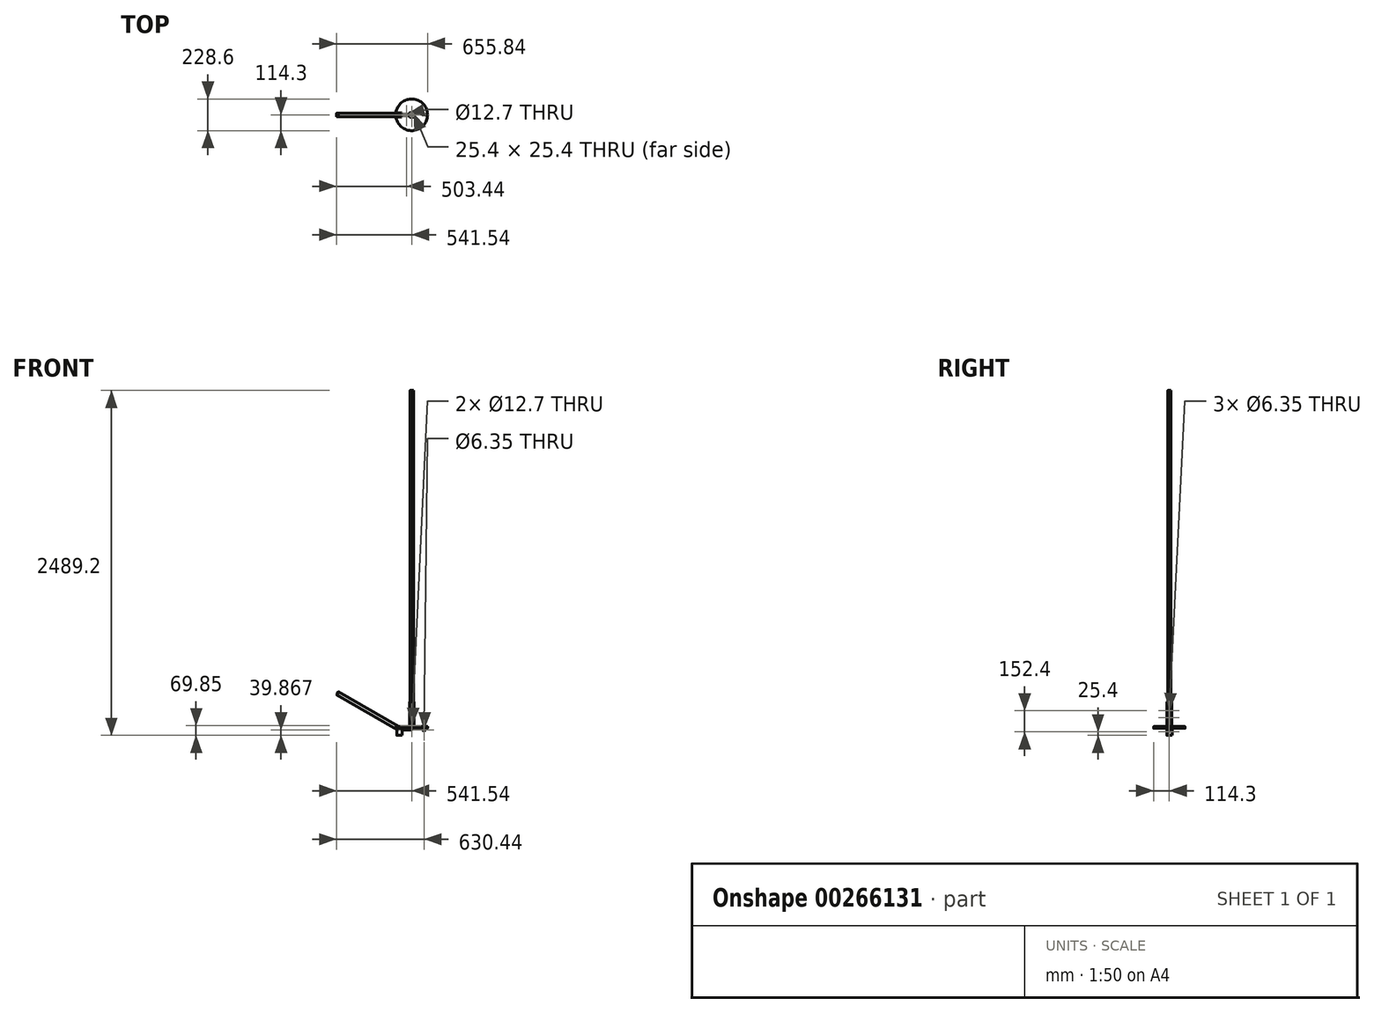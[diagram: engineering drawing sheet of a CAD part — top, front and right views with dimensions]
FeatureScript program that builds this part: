
annotation { "Feature Type Name" : "Feature", "Feature Type Description" : "" }
export const myFeature = defineFeature(function(context is Context, id is Id, definition is map)
    precondition{}
    {
        {
            var Q0;
            Q0=qCreatedBy(makeId("Right.planeOp"),FACE);
            var sketch = newSketch(context, id + "F16", { "sketchPlane" : qUnion([Q0])});
            skLineSegment(sketch, "E0", {"start": v(12.7, 9.53) * mm, "end": v(12.7, -9.53) * mm});
            skLineSegment(sketch, "E1", {"start": v(9.53, -12.7) * mm, "end": v(-9.53, -12.7) * mm});
            skLineSegment(sketch, "E2", {"start": v(-12.7, -9.53) * mm, "end": v(-12.7, 9.53) * mm});
            skLineSegment(sketch, "E3", {"start": v(-9.52, 12.7) * mm, "end": v(9.52, 12.7) * mm});
            skPoint(sketch, "E4.visualSharp", {"position": v(-12.7, 12.7) * mm});
            skArc(sketch, "E4.filletArc", {"start": v(-9.52, 12.7) * mm, "mid": v(-11.77, 11.77) * mm, "end": v(-12.7, 9.53) * mm});
            skPoint(sketch, "E5.visualSharp", {"position": v(12.7, 12.7) * mm});
            skArc(sketch, "E5.filletArc", {"start": v(12.7, 9.53) * mm, "mid": v(11.77, 11.77) * mm, "end": v(9.52, 12.7) * mm});
            skPoint(sketch, "E6.visualSharp", {"position": v(12.7, -12.7) * mm});
            skArc(sketch, "E6.filletArc", {"start": v(9.53, -12.7) * mm, "mid": v(11.77, -11.77) * mm, "end": v(12.7, -9.53) * mm});
            skPoint(sketch, "E7.visualSharp", {"position": v(-12.7, -12.7) * mm});
            skArc(sketch, "E7.filletArc", {"start": v(-12.7, -9.53) * mm, "mid": v(-11.77, -11.77) * mm, "end": v(-9.53, -12.7) * mm});
            skLineSegment(sketch, "E8.0", {"start": v(-9.52, 9.53) * mm, "end": v(9.52, 9.53) * mm});
            skLineSegment(sketch, "E9.0", {"start": v(9.53, 9.53) * mm, "end": v(9.53, -9.53) * mm});
            skLineSegment(sketch, "E10.0", {"start": v(-9.53, -9.53) * mm, "end": v(-9.53, 9.53) * mm});
            skLineSegment(sketch, "E11.0", {"start": v(9.52, -9.53) * mm, "end": v(-9.53, -9.53) * mm});
            skSolve(sketch);
        }
        {
            var Q0;
            Q0=qCreatedBy(makeId("Front.planeOp"),FACE);
            var sketch = newSketch(context, id + "F0", { "sketchPlane" : qUnion([Q0])});
            skLineSegment(sketch, "E12", {"start": v(0, 0) * mm, "end": v(0, -12.7) * mm, "construction": true});
            skLineSegment(sketch, "E13", {"start": v(0, -12.7) * mm, "end": v(-94.8, -12.7) * mm});
            skLineSegment(sketch, "E14", {"start": v(-107.5, -9.3) * mm, "end": v(-541.54, 241.3) * mm});
            skPoint(sketch, "E15.visualSharp", {"position": v(-101.6, -12.7) * mm});
            skArc(sketch, "E15.filletArc", {"start": v(-107.5, -9.3) * mm, "mid": v(-101.37, -11.83) * mm, "end": v(-94.8, -12.7) * mm});
            skSolve(sketch);
        }
        {
            var Q0;
            Q0=makeQuery(id+"F16.imprint","IMPRINT",FACE,{"disambiguationData":[TD([[makeQuery(id+"F16.imprint","IMPRINT",EDGE,{"derivedFrom":sQuery(id+"F16.wireOp",EDGE,"E0")}),-1.0]])]});
            var Q1;
            Q1=sQuery(id+"F0.wireOp",EDGE,"E13");
            var Q2;
            Q2=sQuery(id+"F0.wireOp",EDGE,"E15.filletArc");
            var Q3;
            Q3=sQuery(id+"F0.wireOp",EDGE,"E14");
            sweep(context, id + "F1", {"profiles" : qUnion([Q0]), "path" : qUnion([Q1, Q2, Q3])});
        }
        {
            var Q0;
            Q0=makeQuery(id+"F1.opSweep","SWEPT_FACE",FACE,{"disambiguationData":[OSD([sQuery(id+"F16.wireOp",EDGE,"E2"),sQuery(id+"F0.wireOp",EDGE,"E14")])]});
            var sketch = newSketch(context, id + "F17", { "sketchPlane" : qUnion([Q0])});
            skCircle(sketch, "E16", {"center": v(-518.7, 242.77) * mm, "radius": 4.13 * mm});
            skCircle(sketch, "E17", {"center": v(-463.7, 211.02) * mm, "radius": 4.13 * mm});
            skLineSegment(sketch, "E18", {"start": v(-539.95, 244.05) * mm, "end": v(-530.43, 260.55) * mm, "construction": true});
            skSolve(sketch);
        }
        {
            var Q0;
            Q0=makeQuery(id+"F17.imprint","IMPRINT",FACE,{"disambiguationData":[TD([[makeQuery(id+"F17.imprint","IMPRINT",EDGE,{"derivedFrom":sQuery(id+"F17.wireOp",EDGE,"E16")}),1.0]])]});
            var Q1;
            Q1=makeQuery(id+"F17.imprint","IMPRINT",FACE,{"disambiguationData":[TD([[makeQuery(id+"F17.imprint","IMPRINT",EDGE,{"derivedFrom":sQuery(id+"F17.wireOp",EDGE,"E17")}),1.0]])]});
            extrude(context, id + "F2", {"entities" : qUnion([Q0, Q1]), "operationType" : NewBodyOperationType.REMOVE, "oppositeDirection" : true, "depth" : 25.4 * mm});
        }
        {
            var Q0;
            Q0=makeQuery(id+"F1.opSweep","SWEPT_FACE",FACE,{"disambiguationData":[OSD([sQuery(id+"F16.wireOp",EDGE,"E3"),sQuery(id+"F0.wireOp",EDGE,"E13")])]});
            var sketch = newSketch(context, id + "F3", { "sketchPlane" : qUnion([Q0])});
            skCircle(sketch, "E19", {"center": v(-38.1, 0) * mm, "radius": 6.35 * mm});
            skSolve(sketch);
        }
        {
            var Q0;
            Q0=makeQuery(id+"F3.imprint","IMPRINT",FACE,{"disambiguationData":[TD([[makeQuery(id+"F3.imprint","IMPRINT",EDGE,{"derivedFrom":sQuery(id+"F3.wireOp",EDGE,"E19")}),1.0]])]});
            extrude(context, id + "F18", {"entities" : qUnion([Q0]), "operationType" : NewBodyOperationType.REMOVE, "oppositeDirection" : true, "depth" : 25.4 * mm});
        }
        {
            var Q0;
            Q0=qCreatedBy(makeId("Top.planeOp"),FACE);
            var sketch = newSketch(context, id + "F4", { "sketchPlane" : qUnion([Q0])});
            skLineSegment(sketch, "E20", {"start": v(12.7, 15.88) * mm, "end": v(-12.7, 15.88) * mm});
            skLineSegment(sketch, "E21", {"start": v(-15.87, 12.7) * mm, "end": v(-15.87, -12.7) * mm});
            skLineSegment(sketch, "E22", {"start": v(-12.7, -15.88) * mm, "end": v(12.7, -15.87) * mm});
            skLineSegment(sketch, "E23", {"start": v(15.88, -12.7) * mm, "end": v(15.88, 12.7) * mm});
            skPoint(sketch, "E24.visualSharp", {"position": v(-15.87, 15.88) * mm});
            skArc(sketch, "E24.filletArc", {"start": v(-12.7, 15.87) * mm, "mid": v(-14.95, 14.95) * mm, "end": v(-15.87, 12.7) * mm});
            skPoint(sketch, "E25.visualSharp", {"position": v(15.88, 15.88) * mm});
            skArc(sketch, "E25.filletArc", {"start": v(15.88, 12.7) * mm, "mid": v(14.95, 14.95) * mm, "end": v(12.7, 15.88) * mm});
            skPoint(sketch, "E26.visualSharp", {"position": v(15.88, -15.87) * mm});
            skArc(sketch, "E26.filletArc", {"start": v(12.7, -15.87) * mm, "mid": v(14.95, -14.95) * mm, "end": v(15.88, -12.7) * mm});
            skPoint(sketch, "E27.visualSharp", {"position": v(-15.87, -15.87) * mm});
            skArc(sketch, "E27.filletArc", {"start": v(-15.87, -12.7) * mm, "mid": v(-14.95, -14.95) * mm, "end": v(-12.7, -15.88) * mm});
            skLineSegment(sketch, "E28.0", {"start": v(12.7, 12.7) * mm, "end": v(-12.7, 12.7) * mm});
            skLineSegment(sketch, "E29.0", {"start": v(12.7, -12.7) * mm, "end": v(12.7, 12.7) * mm});
            skLineSegment(sketch, "E30.0", {"start": v(-12.7, -12.7) * mm, "end": v(12.7, -12.7) * mm});
            skLineSegment(sketch, "E31.0", {"start": v(-12.7, 12.7) * mm, "end": v(-12.7, -12.7) * mm});
            skSolve(sketch);
        }
        {
            var Q0;
            Q0=makeQuery(id+"F4.imprint","IMPRINT",FACE,{"disambiguationData":[TD([[makeQuery(id+"F4.imprint","IMPRINT",EDGE,{"derivedFrom":sQuery(id+"F4.wireOp",EDGE,"E20")}),1.0]])]});
            extrude(context, id + "F5", {"entities" : qUnion([Q0]), "depth" : 190.5 * mm});
        }
        {
            var Q0;
            Q0=makeQuery(id+"F5.opExtrude","SWEPT_FACE",FACE,{"disambiguationData":[OSD([sQuery(id+"F4.wireOp",EDGE,"E22")])]});
            var sketch = newSketch(context, id + "F6", { "sketchPlane" : qUnion([Q0])});
            skCircle(sketch, "E32", {"center": v(0, 19.05) * mm, "radius": 6.35 * mm});
            skSolve(sketch);
        }
        {
            var Q0;
            Q0=makeQuery(id+"F6.imprint","IMPRINT",FACE,{"disambiguationData":[TD([[makeQuery(id+"F6.imprint","IMPRINT",EDGE,{"derivedFrom":sQuery(id+"F6.wireOp",EDGE,"E32")}),1.0]])]});
            extrude(context, id + "F19", {"entities" : qUnion([Q0]), "operationType" : NewBodyOperationType.REMOVE, "oppositeDirection" : true, "depth" : 31.75 * mm});
        }
        {
            var Q0;
            Q0=makeQuery(id+"F5.opExtrude","SWEPT_FACE",FACE,{"disambiguationData":[OSD([sQuery(id+"F4.wireOp",EDGE,"E21")])]});
            var sketch = newSketch(context, id + "F7", { "sketchPlane" : qUnion([Q0])});
            skCircle(sketch, "E33", {"center": v(0, 127) * mm, "radius": 3.18 * mm});
            skCircle(sketch, "E34", {"center": v(0, 76.2) * mm, "radius": 3.18 * mm});
            skSolve(sketch);
        }
        {
            var Q0;
            Q0=makeQuery(id+"F7.imprint","IMPRINT",FACE,{"disambiguationData":[TD([[makeQuery(id+"F7.imprint","IMPRINT",EDGE,{"derivedFrom":sQuery(id+"F7.wireOp",EDGE,"E33")}),1.0]])]});
            var Q1;
            Q1=makeQuery(id+"F7.imprint","IMPRINT",FACE,{"disambiguationData":[TD([[makeQuery(id+"F7.imprint","IMPRINT",EDGE,{"derivedFrom":sQuery(id+"F7.wireOp",EDGE,"E34")}),1.0]])]});
            extrude(context, id + "F8", {"entities" : qUnion([Q0, Q1]), "operationType" : NewBodyOperationType.REMOVE, "oppositeDirection" : true, "depth" : 3.17 * mm});
        }
        {
            var Q0;
            Q0=qCreatedBy(makeId("Top.planeOp"),FACE);
            var sketch = newSketch(context, id + "F9", { "sketchPlane" : qUnion([Q0])});
            skCircle(sketch, "E35", {"center": v(0, 0) * mm, "radius": 114.3 * mm});
            skLineSegment(sketch, "E36", {"start": v(-101.6, 12.7) * mm, "end": v(-76.2, 12.7) * mm});
            skLineSegment(sketch, "E37", {"start": v(-76.2, 12.7) * mm, "end": v(-76.2, -12.7) * mm});
            skLineSegment(sketch, "E38", {"start": v(-76.2, -12.7) * mm, "end": v(-101.6, -12.7) * mm});
            skLineSegment(sketch, "E39", {"start": v(-101.6, -12.7) * mm, "end": v(-101.6, 12.7) * mm});
            skLineSegment(sketch, "E40", {"start": v(-104.78, 15.88) * mm, "end": v(-73.03, 15.88) * mm, "construction": true});
            skLineSegment(sketch, "E41", {"start": v(-73.03, 15.88) * mm, "end": v(-73.03, -15.87) * mm, "construction": true});
            skLineSegment(sketch, "E42", {"start": v(-73.03, -15.87) * mm, "end": v(-104.78, -15.88) * mm, "construction": true});
            skLineSegment(sketch, "E43", {"start": v(-104.78, -15.88) * mm, "end": v(-104.78, 15.88) * mm, "construction": true});
            skSolve(sketch);
        }
        {
            var Q0;
            Q0=makeQuery(id+"F9.imprint","IMPRINT",FACE,{"disambiguationData":[TD([[makeQuery(id+"F9.imprint","IMPRINT",EDGE,{"derivedFrom":sQuery(id+"F9.wireOp",EDGE,"E35")}),1.0]])]});
            extrude(context, id + "F10", {"entities" : qUnion([Q0]), "depth" : 12.7 * mm});
        }
        {
            var Q0;
            Q0=makeQuery(id+"F10.opExtrude","CAP_FACE",FACE,{"disambiguationData":[OSD([sQuery(id+"F9.wireOp",EDGE,"E35"),sQuery(id+"F9.wireOp",EDGE,"E36"),sQuery(id+"F9.wireOp",EDGE,"E37"),sQuery(id+"F9.wireOp",EDGE,"E38"),sQuery(id+"F9.wireOp",EDGE,"E39")])],"isStart":true});
            var sketch = newSketch(context, id + "F20", { "sketchPlane" : qUnion([Q0])});
            skLineSegment(sketch, "E44", {"start": v(-104.78, 15.88) * mm, "end": v(-73.03, 15.88) * mm});
            skLineSegment(sketch, "E45", {"start": v(-73.03, 15.88) * mm, "end": v(-73.03, -15.87) * mm});
            skLineSegment(sketch, "E46", {"start": v(-73.03, -15.88) * mm, "end": v(-104.78, -15.88) * mm});
            skLineSegment(sketch, "E47", {"start": v(-104.78, -15.88) * mm, "end": v(-104.78, 15.88) * mm});
            skLineSegment(sketch, "E48", {"start": v(-69.85, -19.05) * mm, "end": v(-107.95, -19.05) * mm});
            skLineSegment(sketch, "E49", {"start": v(-107.95, -19.05) * mm, "end": v(-107.95, 19.05) * mm});
            skLineSegment(sketch, "E50", {"start": v(-107.95, 19.05) * mm, "end": v(-69.85, 19.05) * mm});
            skLineSegment(sketch, "E51", {"start": v(-69.85, 19.05) * mm, "end": v(-69.85, -19.05) * mm});
            skSolve(sketch);
        }
        {
            var Q0;
            Q0=makeQuery(id+"F20.imprint","IMPRINT",FACE,{"disambiguationData":[TD([[makeQuery(id+"F20.imprint","IMPRINT",EDGE,{"derivedFrom":sQuery(id+"F20.wireOp",EDGE,"E44")}),1.0]])]});
            extrude(context, id + "F11", {"entities" : qUnion([Q0]), "operationType" : NewBodyOperationType.ADD, "depth" : 50.8 * mm});
        }
        {
            var Q0;
            Q0=makeQuery(id+"F11.opExtrude","SWEPT_FACE",FACE,{"disambiguationData":[OSD([sQuery(id+"F20.wireOp",EDGE,"E49")])]});
            var sketch = newSketch(context, id + "F12", { "sketchPlane" : qUnion([Q0])});
            skCircle(sketch, "E52", {"center": v(0, -25.4) * mm, "radius": 3.18 * mm});
            skSolve(sketch);
        }
        {
            var Q0;
            Q0=makeQuery(id+"F12.imprint","IMPRINT",FACE,{"disambiguationData":[TD([[makeQuery(id+"F12.imprint","IMPRINT",EDGE,{"derivedFrom":sQuery(id+"F12.wireOp",EDGE,"E52")}),1.0]])]});
            extrude(context, id + "F21", {"entities" : qUnion([Q0]), "operationType" : NewBodyOperationType.REMOVE, "oppositeDirection" : true, "depth" : 3.17 * mm});
        }
        {
            var Q0;
            Q0=makeQuery(id+"F11.opExtrude","SWEPT_EDGE",EDGE,{"disambiguationData":[OSD([sQuery(id+"F20.wireOp",EDGE,"E48"),sQuery(id+"F20.wireOp",EDGE,"E49")])]});
            var Q1;
            Q1=makeQuery(id+"F11.opExtrude","SWEPT_EDGE",EDGE,{"disambiguationData":[OSD([sQuery(id+"F20.wireOp",EDGE,"E49"),sQuery(id+"F20.wireOp",EDGE,"E50")])]});
            var Q2;
            Q2=makeQuery(id+"F11.opExtrude","SWEPT_EDGE",EDGE,{"disambiguationData":[OSD([sQuery(id+"F20.wireOp",EDGE,"E48"),sQuery(id+"F20.wireOp",EDGE,"E51")])]});
            var Q3;
            Q3=makeQuery(id+"F11.opExtrude","SWEPT_EDGE",EDGE,{"disambiguationData":[OSD([sQuery(id+"F20.wireOp",EDGE,"E50"),sQuery(id+"F20.wireOp",EDGE,"E51")])]});
            var Q4;
            Q4=makeQuery(id+"F10.opExtrude","CAP_EDGE",EDGE,{"disambiguationData":[OSD([sQuery(id+"F9.wireOp",EDGE,"E35")])],"isStart":true});
            var Q5;
            Q5=makeQuery(id+"F10.opExtrude","CAP_EDGE",EDGE,{"disambiguationData":[OSD([sQuery(id+"F9.wireOp",EDGE,"E35")])],"isStart":false});
            fillet(context, id + "F13", {"entities" : qUnion([Q0, Q1, Q2, Q3, Q4, Q5]), "radius" : 1.59 * mm, "tangentPropagation" : true, "allowEdgeOverflow" : false});
        }
        {
            var Q0;
            Q0=qCreatedBy(makeId("Front.planeOp"),FACE);
            var sketch = newSketch(context, id + "F22", { "sketchPlane" : qUnion([Q0])});
            skLineSegment(sketch, "E53", {"start": v(73.03, 0) * mm, "end": v(84.02, -19.05) * mm});
            skLineSegment(sketch, "E54", {"start": v(84.02, -19.05) * mm, "end": v(93.78, -19.05) * mm, "construction": true});
            skLineSegment(sketch, "E55", {"start": v(93.78, -19.05) * mm, "end": v(104.78, 0) * mm});
            skLineSegment(sketch, "E56", {"start": v(104.78, 0) * mm, "end": v(73.03, 0) * mm});
            skArc(sketch, "E57", {"start": v(84.02, -19.05) * mm, "mid": v(88.9, -21.87) * mm, "end": v(93.78, -19.05) * mm});
            skLineSegment(sketch, "E58", {"start": v(88.9, 0) * mm, "end": v(88.9, -21.87) * mm, "construction": true});
            skCircle(sketch, "E59", {"center": v(88.9, -10.93) * mm, "radius": 3.18 * mm});
            skSolve(sketch);
        }
        {
            var Q0;
            Q0=makeQuery(id+"F22.imprint","IMPRINT",FACE,{"disambiguationData":[TD([[makeQuery(id+"F22.imprint","IMPRINT",EDGE,{"derivedFrom":sQuery(id+"F22.wireOp",EDGE,"E53")}),1.0]])]});
            extrude(context, id + "F14", {"entities" : qUnion([Q0]), "operationType" : NewBodyOperationType.ADD, "endBound" : BoundingType.SYMMETRIC, "depth" : 7.87 * mm});
        }
        {
            var Q0;
            Q0=qCreatedBy(makeId("Top.planeOp"),FACE);
            var sketch = newSketch(context, id + "F23", { "sketchPlane" : qUnion([Q0])});
            skLineSegment(sketch, "E60", {"start": v(0, 0) * mm, "end": v(12.7, 12.7) * mm, "construction": true});
            skLineSegment(sketch, "E61", {"start": v(9.53, 12.7) * mm, "end": v(3.56, 12.7) * mm});
            skLineSegment(sketch, "E62", {"start": v(3.18, 12.32) * mm, "end": v(3.18, 11.5) * mm});
            skLineSegment(sketch, "E63", {"start": v(3.56, 11.11) * mm, "end": v(6.92, 11.11) * mm});
            skLineSegment(sketch, "E64", {"start": v(7.82, 8.94) * mm, "end": v(2.8, 3.92) * mm});
            skLineSegment(sketch, "E65", {"start": v(1, 3.18) * mm, "end": v(0, 3.18) * mm});
            skLineSegment(sketch, "E66.MirrorCS", {"start": v(3.18, 1) * mm, "end": v(3.18, 0) * mm});
            skLineSegment(sketch, "E67.MirrorCS", {"start": v(8.94, 7.82) * mm, "end": v(3.92, 2.8) * mm});
            skLineSegment(sketch, "E68.MirrorCS", {"start": v(12.7, 9.53) * mm, "end": v(12.7, 3.56) * mm});
            skLineSegment(sketch, "E69.MirrorCS", {"start": v(11.11, 3.56) * mm, "end": v(11.11, 6.92) * mm});
            skLineSegment(sketch, "E70.MirrorCS", {"start": v(12.32, 3.18) * mm, "end": v(11.5, 3.18) * mm});
            skLineSegment(sketch, "E71.1.0", {"start": v(-11.11, 3.56) * mm, "end": v(-11.11, 6.92) * mm});
            skLineSegment(sketch, "E71.1.1", {"start": v(-7.82, 8.94) * mm, "end": v(-2.8, 3.92) * mm});
            skLineSegment(sketch, "E71.1.2", {"start": v(-1, 3.18) * mm, "end": v(0, 3.18) * mm});
            skLineSegment(sketch, "E71.1.3", {"start": v(-12.7, 9.53) * mm, "end": v(-12.7, 3.56) * mm});
            skLineSegment(sketch, "E71.1.4", {"start": v(-3.18, 1) * mm, "end": v(-3.18, 0) * mm});
            skLineSegment(sketch, "E71.1.5", {"start": v(-8.94, 7.82) * mm, "end": v(-3.92, 2.8) * mm});
            skLineSegment(sketch, "E71.1.6", {"start": v(-3.56, 11.11) * mm, "end": v(-6.92, 11.11) * mm});
            skLineSegment(sketch, "E71.1.7", {"start": v(-3.18, 12.32) * mm, "end": v(-3.18, 11.5) * mm});
            skLineSegment(sketch, "E71.1.8", {"start": v(-12.32, 3.18) * mm, "end": v(-11.5, 3.18) * mm});
            skLineSegment(sketch, "E71.1.9", {"start": v(-9.53, 12.7) * mm, "end": v(-3.56, 12.7) * mm});
            skLineSegment(sketch, "E71.2.0", {"start": v(-3.56, -11.11) * mm, "end": v(-6.92, -11.11) * mm});
            skLineSegment(sketch, "E71.2.1", {"start": v(-8.94, -7.82) * mm, "end": v(-3.92, -2.8) * mm});
            skLineSegment(sketch, "E71.2.2", {"start": v(-3.18, -1) * mm, "end": v(-3.18, 0) * mm});
            skLineSegment(sketch, "E71.2.3", {"start": v(-9.53, -12.7) * mm, "end": v(-3.56, -12.7) * mm});
            skLineSegment(sketch, "E71.2.4", {"start": v(-1, -3.18) * mm, "end": v(0, -3.18) * mm});
            skLineSegment(sketch, "E71.2.5", {"start": v(-7.82, -8.94) * mm, "end": v(-2.8, -3.92) * mm});
            skLineSegment(sketch, "E71.2.6", {"start": v(-11.11, -3.56) * mm, "end": v(-11.11, -6.92) * mm});
            skLineSegment(sketch, "E71.2.7", {"start": v(-12.32, -3.18) * mm, "end": v(-11.5, -3.18) * mm});
            skLineSegment(sketch, "E71.2.8", {"start": v(-3.18, -12.32) * mm, "end": v(-3.18, -11.5) * mm});
            skLineSegment(sketch, "E71.2.9", {"start": v(-12.7, -9.53) * mm, "end": v(-12.7, -3.56) * mm});
            skLineSegment(sketch, "E71.3.0", {"start": v(11.11, -3.56) * mm, "end": v(11.11, -6.92) * mm});
            skLineSegment(sketch, "E71.3.1", {"start": v(7.82, -8.94) * mm, "end": v(2.8, -3.92) * mm});
            skLineSegment(sketch, "E71.3.2", {"start": v(1, -3.18) * mm, "end": v(0, -3.18) * mm});
            skLineSegment(sketch, "E71.3.3", {"start": v(12.7, -9.53) * mm, "end": v(12.7, -3.56) * mm});
            skLineSegment(sketch, "E71.3.4", {"start": v(3.17, -1) * mm, "end": v(3.17, 0) * mm});
            skLineSegment(sketch, "E71.3.5", {"start": v(8.94, -7.82) * mm, "end": v(3.92, -2.8) * mm});
            skLineSegment(sketch, "E71.3.6", {"start": v(3.56, -11.11) * mm, "end": v(6.92, -11.11) * mm});
            skLineSegment(sketch, "E71.3.7", {"start": v(3.18, -12.32) * mm, "end": v(3.18, -11.5) * mm});
            skLineSegment(sketch, "E71.3.8", {"start": v(12.32, -3.18) * mm, "end": v(11.5, -3.18) * mm});
            skLineSegment(sketch, "E71.3.9", {"start": v(9.53, -12.7) * mm, "end": v(3.56, -12.7) * mm});
            skPoint(sketch, "E71.center", {"position": v(0, 0) * mm});
            skPoint(sketch, "E72.visualSharp", {"position": v(-12.7, 12.7) * mm});
            skArc(sketch, "E72.filletArc", {"start": v(-9.53, 12.7) * mm, "mid": v(-11.77, 11.77) * mm, "end": v(-12.7, 9.53) * mm});
            skPoint(sketch, "E73.visualSharp", {"position": v(-12.7, -12.7) * mm});
            skArc(sketch, "E73.filletArc", {"start": v(-12.7, -9.53) * mm, "mid": v(-11.77, -11.77) * mm, "end": v(-9.53, -12.7) * mm});
            skPoint(sketch, "E74.visualSharp", {"position": v(12.7, -12.7) * mm});
            skArc(sketch, "E74.filletArc", {"start": v(9.53, -12.7) * mm, "mid": v(11.77, -11.77) * mm, "end": v(12.7, -9.53) * mm});
            skPoint(sketch, "E75.visualSharp", {"position": v(12.7, 12.7) * mm});
            skArc(sketch, "E75.filletArc", {"start": v(12.7, 9.53) * mm, "mid": v(11.77, 11.77) * mm, "end": v(9.53, 12.7) * mm});
            skPoint(sketch, "E76.visualSharp", {"position": v(-2.05, 3.17) * mm});
            skArc(sketch, "E76.filletArc", {"start": v(-2.8, 3.92) * mm, "mid": v(-1.97, 3.37) * mm, "end": v(-1, 3.18) * mm});
            skPoint(sketch, "E77.visualSharp", {"position": v(2.05, 3.18) * mm});
            skArc(sketch, "E77.filletArc", {"start": v(1, 3.18) * mm, "mid": v(1.97, 3.37) * mm, "end": v(2.8, 3.92) * mm});
            skPoint(sketch, "E78.visualSharp", {"position": v(-3.18, 2.05) * mm});
            skArc(sketch, "E78.filletArc", {"start": v(-3.18, 1) * mm, "mid": v(-3.37, 1.97) * mm, "end": v(-3.92, 2.8) * mm});
            skPoint(sketch, "E79.visualSharp", {"position": v(-3.17, -2.05) * mm});
            skArc(sketch, "E79.filletArc", {"start": v(-3.92, -2.8) * mm, "mid": v(-3.37, -1.97) * mm, "end": v(-3.18, -1) * mm});
            skPoint(sketch, "E80.visualSharp", {"position": v(-2.05, -3.18) * mm});
            skArc(sketch, "E80.filletArc", {"start": v(-1, -3.18) * mm, "mid": v(-1.97, -3.37) * mm, "end": v(-2.8, -3.92) * mm});
            skPoint(sketch, "E81.visualSharp", {"position": v(2.05, -3.18) * mm});
            skArc(sketch, "E81.filletArc", {"start": v(2.8, -3.92) * mm, "mid": v(1.97, -3.37) * mm, "end": v(1, -3.18) * mm});
            skPoint(sketch, "E82.visualSharp", {"position": v(3.18, -2.05) * mm});
            skArc(sketch, "E82.filletArc", {"start": v(3.17, -1) * mm, "mid": v(3.37, -1.97) * mm, "end": v(3.92, -2.8) * mm});
            skPoint(sketch, "E83.visualSharp", {"position": v(3.18, 2.05) * mm});
            skArc(sketch, "E83.filletArc", {"start": v(3.92, 2.8) * mm, "mid": v(3.37, 1.97) * mm, "end": v(3.18, 1) * mm});
            skPoint(sketch, "E84.visualSharp", {"position": v(-11.11, -9.99) * mm});
            skArc(sketch, "E84.filletArc", {"start": v(-11.11, -6.92) * mm, "mid": v(-10.33, -8.1) * mm, "end": v(-8.94, -7.82) * mm});
            skPoint(sketch, "E85.visualSharp", {"position": v(-9.99, -11.11) * mm});
            skArc(sketch, "E85.filletArc", {"start": v(-7.82, -8.94) * mm, "mid": v(-8.1, -10.33) * mm, "end": v(-6.92, -11.11) * mm});
            skPoint(sketch, "E86.visualSharp", {"position": v(9.99, -11.11) * mm});
            skArc(sketch, "E86.filletArc", {"start": v(6.92, -11.11) * mm, "mid": v(8.1, -10.33) * mm, "end": v(7.82, -8.94) * mm});
            skPoint(sketch, "E87.visualSharp", {"position": v(11.11, -9.99) * mm});
            skArc(sketch, "E87.filletArc", {"start": v(8.94, -7.82) * mm, "mid": v(10.33, -8.1) * mm, "end": v(11.11, -6.92) * mm});
            skPoint(sketch, "E88.visualSharp", {"position": v(11.11, 9.99) * mm});
            skArc(sketch, "E88.filletArc", {"start": v(11.11, 6.92) * mm, "mid": v(10.33, 8.1) * mm, "end": v(8.94, 7.82) * mm});
            skPoint(sketch, "E89.visualSharp", {"position": v(9.99, 11.11) * mm});
            skArc(sketch, "E89.filletArc", {"start": v(7.82, 8.94) * mm, "mid": v(8.1, 10.33) * mm, "end": v(6.92, 11.11) * mm});
            skPoint(sketch, "E90.visualSharp", {"position": v(-9.99, 11.11) * mm});
            skArc(sketch, "E90.filletArc", {"start": v(-6.92, 11.11) * mm, "mid": v(-8.1, 10.33) * mm, "end": v(-7.82, 8.94) * mm});
            skPoint(sketch, "E91.visualSharp", {"position": v(-11.11, 9.99) * mm});
            skArc(sketch, "E91.filletArc", {"start": v(-8.94, 7.82) * mm, "mid": v(-10.33, 8.1) * mm, "end": v(-11.11, 6.92) * mm});
            skPoint(sketch, "E92.visualSharp", {"position": v(-12.7, 3.18) * mm});
            skArc(sketch, "E92.filletArc", {"start": v(-12.7, 3.56) * mm, "mid": v(-12.59, 3.29) * mm, "end": v(-12.32, 3.17) * mm});
            skPoint(sketch, "E93.visualSharp", {"position": v(-11.11, 3.18) * mm});
            skArc(sketch, "E93.filletArc", {"start": v(-11.5, 3.18) * mm, "mid": v(-11.22, 3.29) * mm, "end": v(-11.11, 3.56) * mm});
            skPoint(sketch, "E94.visualSharp", {"position": v(-12.7, -3.18) * mm});
            skArc(sketch, "E94.filletArc", {"start": v(-12.32, -3.18) * mm, "mid": v(-12.59, -3.29) * mm, "end": v(-12.7, -3.56) * mm});
            skPoint(sketch, "E95.visualSharp", {"position": v(-11.11, -3.18) * mm});
            skArc(sketch, "E95.filletArc", {"start": v(-11.11, -3.56) * mm, "mid": v(-11.22, -3.29) * mm, "end": v(-11.5, -3.18) * mm});
            skPoint(sketch, "E96.visualSharp", {"position": v(-3.18, -11.11) * mm});
            skArc(sketch, "E96.filletArc", {"start": v(-3.18, -11.5) * mm, "mid": v(-3.29, -11.22) * mm, "end": v(-3.56, -11.11) * mm});
            skPoint(sketch, "E97.visualSharp", {"position": v(-3.18, -12.7) * mm});
            skArc(sketch, "E97.filletArc", {"start": v(-3.56, -12.7) * mm, "mid": v(-3.29, -12.59) * mm, "end": v(-3.18, -12.32) * mm});
            skPoint(sketch, "E98.visualSharp", {"position": v(3.18, -11.11) * mm});
            skArc(sketch, "E98.filletArc", {"start": v(3.56, -11.11) * mm, "mid": v(3.29, -11.22) * mm, "end": v(3.18, -11.5) * mm});
            skPoint(sketch, "E99.visualSharp", {"position": v(3.18, -12.7) * mm});
            skArc(sketch, "E99.filletArc", {"start": v(3.18, -12.32) * mm, "mid": v(3.29, -12.59) * mm, "end": v(3.56, -12.7) * mm});
            skPoint(sketch, "E100.visualSharp", {"position": v(12.7, -3.18) * mm});
            skArc(sketch, "E100.filletArc", {"start": v(12.7, -3.56) * mm, "mid": v(12.59, -3.29) * mm, "end": v(12.32, -3.18) * mm});
            skPoint(sketch, "E101.visualSharp", {"position": v(11.11, -3.18) * mm});
            skArc(sketch, "E101.filletArc", {"start": v(11.5, -3.18) * mm, "mid": v(11.22, -3.29) * mm, "end": v(11.11, -3.56) * mm});
            skPoint(sketch, "E102.visualSharp", {"position": v(11.11, 3.18) * mm});
            skArc(sketch, "E102.filletArc", {"start": v(11.11, 3.56) * mm, "mid": v(11.22, 3.29) * mm, "end": v(11.5, 3.18) * mm});
            skPoint(sketch, "E103.visualSharp", {"position": v(12.7, 3.18) * mm});
            skArc(sketch, "E103.filletArc", {"start": v(12.32, 3.18) * mm, "mid": v(12.59, 3.29) * mm, "end": v(12.7, 3.56) * mm});
            skPoint(sketch, "E104.visualSharp", {"position": v(3.18, 11.11) * mm});
            skArc(sketch, "E104.filletArc", {"start": v(3.18, 11.5) * mm, "mid": v(3.29, 11.22) * mm, "end": v(3.56, 11.11) * mm});
            skPoint(sketch, "E105.visualSharp", {"position": v(3.18, 12.7) * mm});
            skArc(sketch, "E105.filletArc", {"start": v(3.56, 12.7) * mm, "mid": v(3.29, 12.59) * mm, "end": v(3.18, 12.32) * mm});
            skPoint(sketch, "E106.visualSharp", {"position": v(-3.18, 12.7) * mm});
            skArc(sketch, "E106.filletArc", {"start": v(-3.18, 12.32) * mm, "mid": v(-3.29, 12.59) * mm, "end": v(-3.56, 12.7) * mm});
            skPoint(sketch, "E107.visualSharp", {"position": v(-3.18, 11.11) * mm});
            skArc(sketch, "E107.filletArc", {"start": v(-3.56, 11.11) * mm, "mid": v(-3.29, 11.22) * mm, "end": v(-3.18, 11.5) * mm});
            skSolve(sketch);
        }
        {
            var Q0;
            Q0=makeQuery(id+"F23.imprint","IMPRINT",FACE,{"disambiguationData":[TD([[makeQuery(id+"F23.imprint","IMPRINT",EDGE,{"derivedFrom":sQuery(id+"F23.wireOp",EDGE,"E61")}),1.0]])]});
            extrude(context, id + "F15", {"entities" : qUnion([Q0]), "depth" : 2438.4 * mm});
        }
    });
